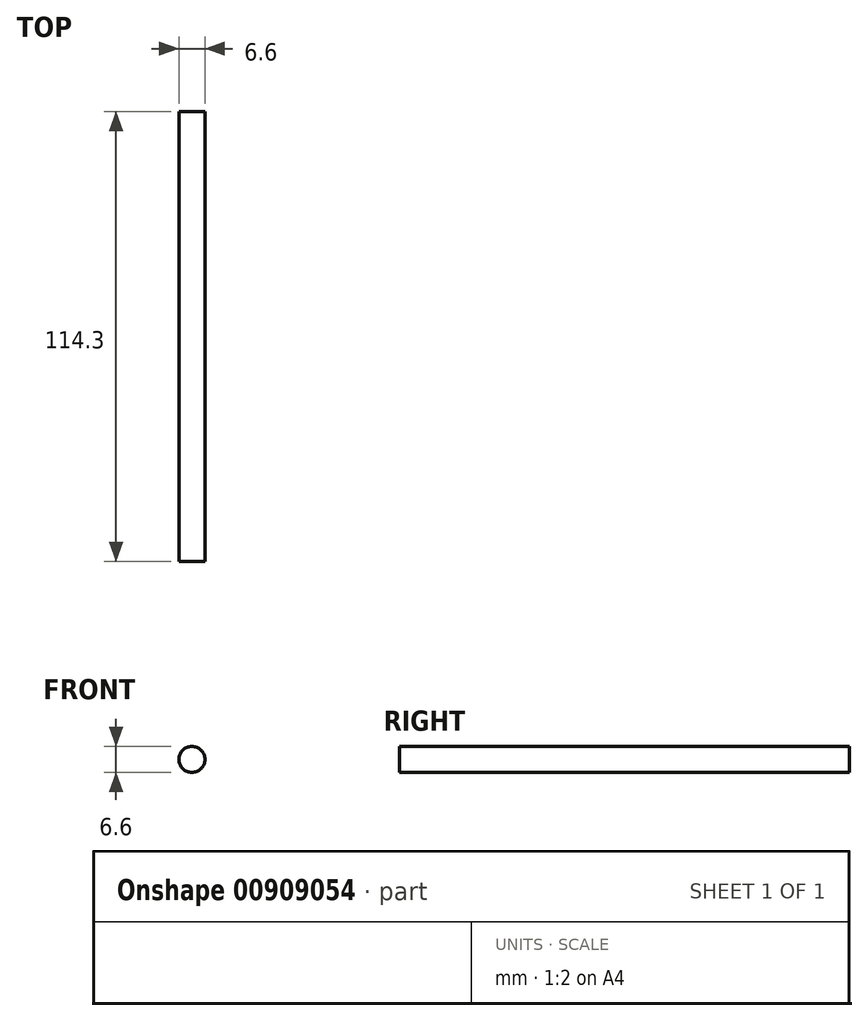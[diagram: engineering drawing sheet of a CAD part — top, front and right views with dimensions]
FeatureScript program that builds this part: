
annotation { "Feature Type Name" : "Feature", "Feature Type Description" : "" }
export const myFeature = defineFeature(function(context is Context, id is Id, definition is map)
    precondition{}
    {
        {
            var Q0;
            Q0=qCreatedBy(makeId("Front.planeOp"),FACE);
            var sketch = newSketch(context, id + "F0", { "sketchPlane" : qUnion([Q0])});
            skCircle(sketch, "E0", {"center": v(0, 0) * mm, "radius": 3.3 * mm});
            skSolve(sketch);
        }
        {
            var Q0;
            Q0=makeQuery(id+"F0.imprint","IMPRINT",FACE,{"disambiguationData":[TD([[makeQuery(id+"F0.imprint","IMPRINT",EDGE,{"derivedFrom":sQuery(id+"F0.wireOp",EDGE,"E0")}),1.0]])]});
            extrude(context, id + "F1", {"entities" : qUnion([Q0]), "depth" : 114.3 * mm, "offsetDistance" : 25.4 * mm});
        }
    });
